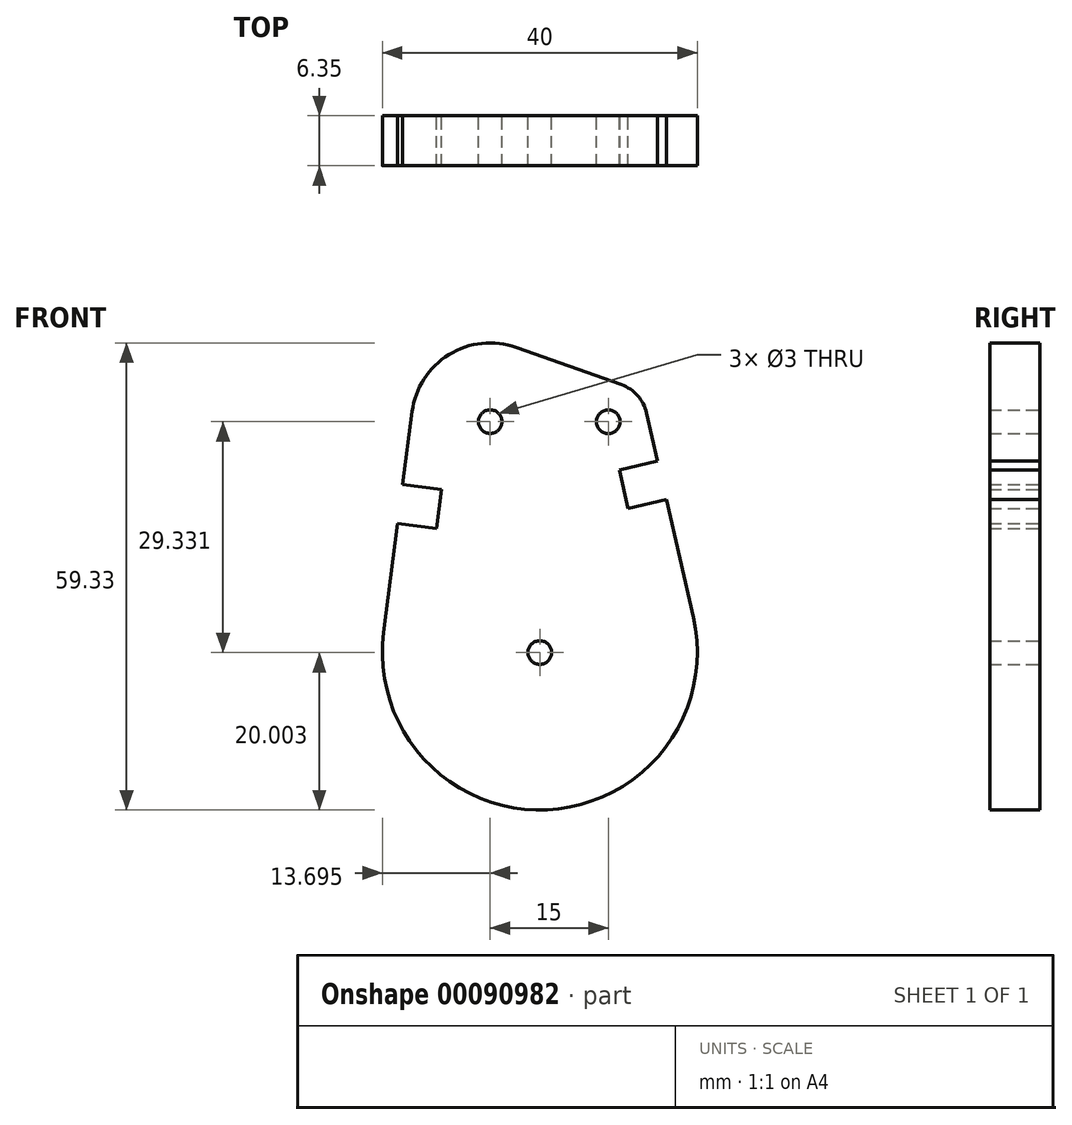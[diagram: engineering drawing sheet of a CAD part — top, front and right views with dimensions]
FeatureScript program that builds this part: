
annotation { "Feature Type Name" : "Feature", "Feature Type Description" : "" }
export const myFeature = defineFeature(function(context is Context, id is Id, definition is map)
    precondition{}
    {
        {
            var Q0;
            Q0=qCreatedBy(makeId("Front.planeOp"),FACE);
            var sketch = newSketch(context, id + "F0", { "sketchPlane" : qUnion([Q0])});
            skCircle(sketch, "E0", {"center": v(-26.27, 43.94) * mm, "radius": 20 * mm});
            skCircle(sketch, "E1", {"center": v(-17.57, 73.26) * mm, "radius": 5 * mm});
            skCircle(sketch, "E2", {"center": v(-32.57, 73.27) * mm, "radius": 10 * mm});
            skLineSegment(sketch, "E3", {"start": v(-42.5, 74.55) * mm, "end": v(-43.69, 65.3) * mm});
            skLineSegment(sketch, "E4", {"start": v(-29.23, 82.7) * mm, "end": v(-15.9, 77.97) * mm});
            skLineSegment(sketch, "E5", {"start": v(-12.7, 74.37) * mm, "end": v(-11.3, 68.25) * mm});
            skLineSegment(sketch, "E6", {"start": v(-11.3, 68.25) * mm, "end": v(-16.18, 67.14) * mm});
            skLineSegment(sketch, "E7", {"start": v(-16.18, 67.14) * mm, "end": v(-15.07, 62.27) * mm});
            skLineSegment(sketch, "E8", {"start": v(-15.07, 62.27) * mm, "end": v(-10.2, 63.38) * mm});
            skLineSegment(sketch, "E9", {"start": v(-43.69, 65.3) * mm, "end": v(-38.73, 64.65) * mm});
            skLineSegment(sketch, "E10", {"start": v(-38.73, 64.65) * mm, "end": v(-39.37, 59.7) * mm});
            skLineSegment(sketch, "E11", {"start": v(-39.37, 59.7) * mm, "end": v(-44.32, 60.33) * mm});
            skLineSegment(sketch, "E12.trimOffspring", {"start": v(-44.32, 60.33) * mm, "end": v(-46.1, 46.5) * mm});
            skLineSegment(sketch, "E13.trimOffspring", {"start": v(-10.2, 63.38) * mm, "end": v(-6.77, 48.4) * mm});
            skCircle(sketch, "E14", {"center": v(-32.57, 73.27) * mm, "radius": 1.5 * mm});
            skCircle(sketch, "E15", {"center": v(-26.27, 43.94) * mm, "radius": 1.5 * mm});
            skCircle(sketch, "E16", {"center": v(-17.57, 73.26) * mm, "radius": 1.5 * mm});
            skSolve(sketch);
        }
        {
            var Q0;
            {var subQ0=sQuery(id+"F0.wireOp",EDGE,"E3");Q0=makeQuery(id+"F0.imprint","IMPRINT",FACE,{"disambiguationData":[TD([[makeQuery(id+"F0.imprint","IMPRINT",EDGE,{"derivedFrom":subQ0}),1.0]])]});}
            var Q1;
            Q1=makeQuery(id+"F0.imprint","IMPRINT",FACE,{"disambiguationData":[TD([[makeQuery(id+"F0.imprint","IMPRINT",EDGE,{"derivedFrom":sQuery(id+"F0.wireOp",EDGE,"E14")}),-1.0]])]});
            var Q2;
            {var subQ0=sQuery(id+"F0.wireOp",EDGE,"E5");Q2=makeQuery(id+"F0.imprint","IMPRINT",FACE,{"disambiguationData":[TD([[makeQuery(id+"F0.imprint","IMPRINT",EDGE,{"derivedFrom":subQ0}),-1.0]])]});}
            var Q3;
            {var subQ0=sQuery(id+"F0.wireOp",EDGE,"E4");Q3=makeQuery(id+"F0.imprint","IMPRINT",FACE,{"disambiguationData":[TD([[makeQuery(id+"F0.imprint","IMPRINT",EDGE,{"derivedFrom":subQ0}),-1.0]])]});}
            var Q4;
            Q4=makeQuery(id+"F0.imprint","IMPRINT",FACE,{"disambiguationData":[TD([[makeQuery(id+"F0.imprint","IMPRINT",EDGE,{"derivedFrom":sQuery(id+"F0.wireOp",EDGE,"E15")}),-1.0]])]});
            var Q5;
            Q5=makeQuery(id+"F0.imprint","IMPRINT",FACE,{"disambiguationData":[TD([[makeQuery(id+"F0.imprint","IMPRINT",EDGE,{"derivedFrom":sQuery(id+"F0.wireOp",EDGE,"E16")}),-1.0]])]});
            var Q6;
            Q6=sQuery(id+"F0.wireOp",EDGE,"E13.trimOffspring");
            var Q7;
            Q7=sQuery(id+"F0.wireOp",EDGE,"E5");
            var Q8;
            Q8=sQuery(id+"F0.wireOp",EDGE,"E4");
            var Q9;
            Q9=sQuery(id+"F0.wireOp",EDGE,"E3");
            var Q10;
            Q10=sQuery(id+"F0.wireOp",EDGE,"E1");
            var Q11;
            Q11=sQuery(id+"F0.wireOp",EDGE,"E12.trimOffspring");
            var Q12;
            Q12=sQuery(id+"F0.wireOp",EDGE,"E0");
            var Q13;
            Q13=sQuery(id+"F0.wireOp",EDGE,"E2");
            var Q14;
            Q14=sQuery(id+"F0.wireOp",EDGE,"E14");
            var Q15;
            Q15=sQuery(id+"F0.wireOp",EDGE,"E16");
            var Q16;
            Q16=sQuery(id+"F0.wireOp",EDGE,"E11");
            var Q17;
            Q17=sQuery(id+"F0.wireOp",EDGE,"E10");
            var Q18;
            Q18=sQuery(id+"F0.wireOp",EDGE,"E9");
            var Q19;
            Q19=sQuery(id+"F0.wireOp",EDGE,"E8");
            var Q20;
            Q20=sQuery(id+"F0.wireOp",EDGE,"E7");
            var Q21;
            Q21=sQuery(id+"F0.wireOp",EDGE,"E6");
            var Q22;
            Q22=sQuery(id+"F0.wireOp",EDGE,"E15");
            extrude(context, id + "F1", {"entities" : qUnion([Q0, Q1, Q2, Q3, Q4, Q5]), "surfaceEntities" : qUnion([Q6, Q7, Q8, Q9, Q10, Q11, Q12, Q13, Q14, Q15, Q16, Q17, Q18, Q19, Q20, Q21, Q22]), "depth" : 6.35 * mm});
        }
    });
